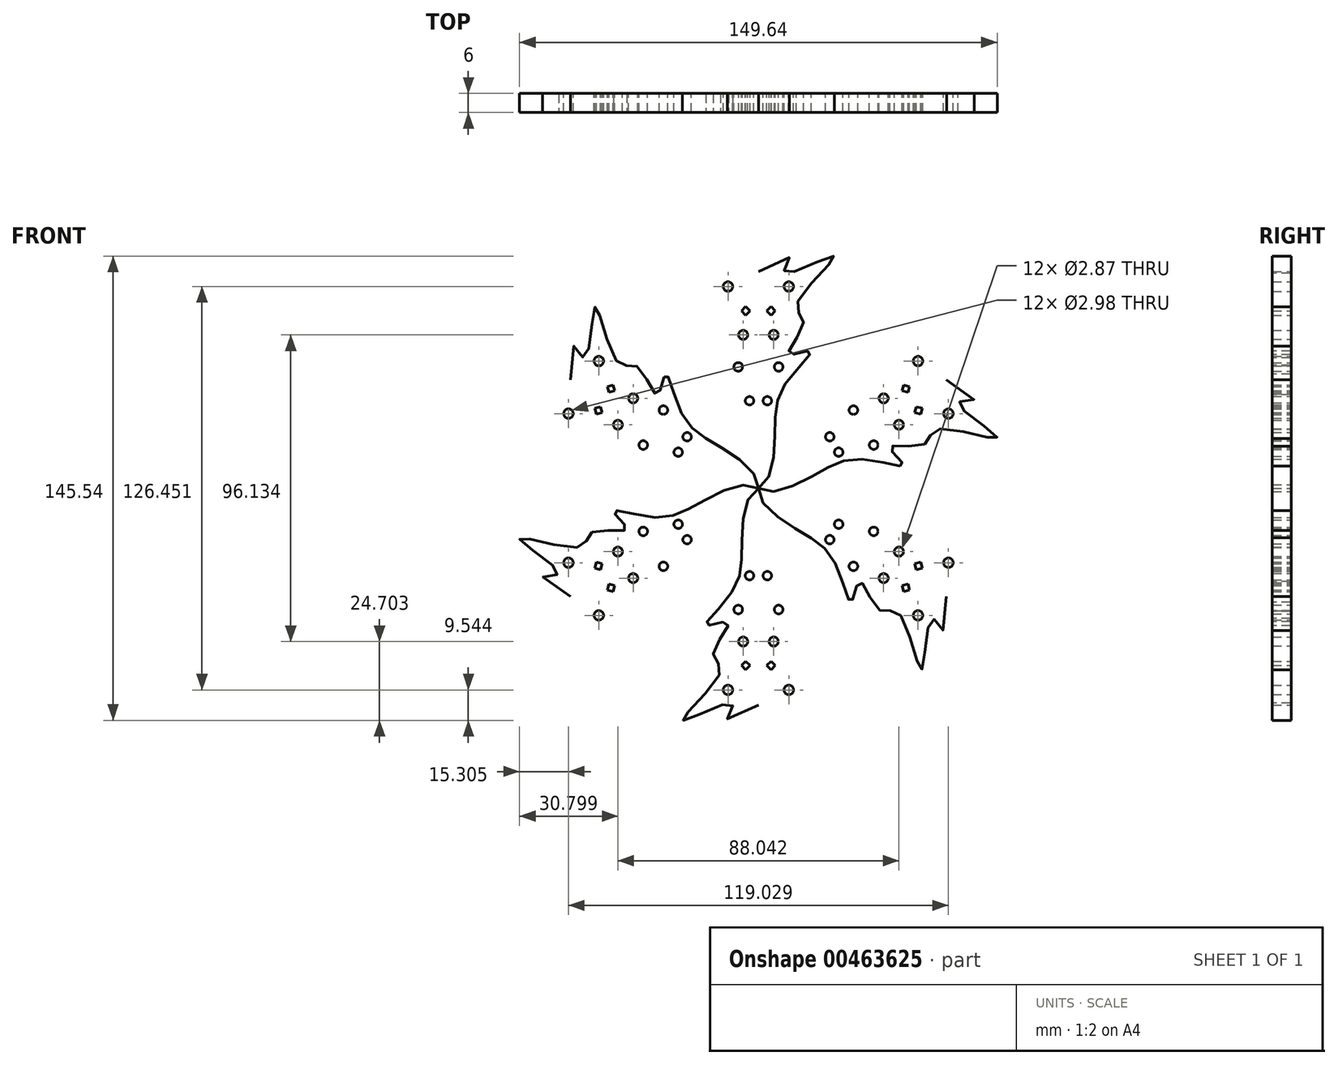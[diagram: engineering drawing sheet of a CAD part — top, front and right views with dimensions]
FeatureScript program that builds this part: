
annotation { "Feature Type Name" : "Feature", "Feature Type Description" : "" }
export const myFeature = defineFeature(function(context is Context, id is Id, definition is map)
    precondition{}
    {
        {
            var Q0;
            Q0=qCreatedBy(makeId("Front.planeOp"),FACE);
            var sketch = newSketch(context, id + "F0", { "sketchPlane" : qUnion([Q0])});
            skLineSegment(sketch, "E0", {"start": v(0, 0) * mm, "end": v(0, 67.96) * mm, "construction": true});
            skFitSpline(sketch, "E1", {"points": [v(0, 67.96) * mm, v(8.04, 67.96) * mm, v(23.58, 72.76) * mm, v(11.93, 57.55) * mm, v(14.13, 51.98) * mm, v(9.52, 42.08) * mm, v(16.32, 43.03) * mm, v(8.31, 32.65) * mm, v(5.2, 16.68) * mm, v(0, 0) * mm], "startDerivative": vector(501.65, 313.3) * mm, "endDerivative": vector(-99, -40.62) * mm});
            skCircle(sketch, "E2", {"center": v(4.79, 48.07) * mm, "radius": 1.43 * mm});
            skCircle(sketch, "E3", {"center": v(6.33, 38.02) * mm, "radius": 1.36 * mm});
            skCircle(sketch, "E4", {"center": v(9.52, 63.23) * mm, "radius": 1.49 * mm});
            skCircle(sketch, "E5", {"center": v(2.79, 27.41) * mm, "radius": 1.33 * mm});
            skLineSegment(sketch, "E6.bottom", {"start": v(3.95, 56.95) * mm, "end": v(5.3, 55.6) * mm});
            skLineSegment(sketch, "E6.top", {"start": v(2.6, 55.6) * mm, "end": v(3.96, 54.24) * mm});
            skLineSegment(sketch, "E6.left", {"start": v(3.95, 56.95) * mm, "end": v(2.6, 55.6) * mm});
            skLineSegment(sketch, "E6.right", {"start": v(5.3, 55.6) * mm, "end": v(3.96, 54.24) * mm});
            skFitSpline(sketch, "E7.MirrorCS", {"points": [v(0, 67.96) * mm, v(-8.04, 67.96) * mm, v(-23.58, 72.76) * mm, v(-11.93, 57.55) * mm, v(-14.13, 51.98) * mm, v(-9.52, 42.08) * mm, v(-16.32, 43.03) * mm, v(-8.31, 32.65) * mm, v(-5.2, 16.68) * mm, v(0, 0) * mm], "startDerivative": vector(-501.65, 313.3) * mm, "endDerivative": vector(99, -40.62) * mm});
            skCircle(sketch, "E8.MirrorC", {"center": v(-9.52, 63.23) * mm, "radius": 1.49 * mm});
            skCircle(sketch, "E9.MirrorC", {"center": v(-4.79, 48.07) * mm, "radius": 1.43 * mm});
            skCircle(sketch, "E10.MirrorC", {"center": v(-6.33, 38.02) * mm, "radius": 1.36 * mm});
            skCircle(sketch, "E11.MirrorC", {"center": v(-2.79, 27.41) * mm, "radius": 1.33 * mm});
            skLineSegment(sketch, "E12.MirrorCS", {"start": v(-2.6, 55.6) * mm, "end": v(-3.96, 54.24) * mm});
            skLineSegment(sketch, "E13.MirrorCS", {"start": v(-3.95, 56.95) * mm, "end": v(-2.6, 55.6) * mm});
            skLineSegment(sketch, "E14.MirrorCS", {"start": v(-3.95, 56.95) * mm, "end": v(-5.3, 55.6) * mm});
            skLineSegment(sketch, "E15.MirrorCS", {"start": v(-5.3, 55.6) * mm, "end": v(-3.96, 54.24) * mm});
            skSolve(sketch);
        }
        {
            var Q0;
            Q0 = qSketchRegion(id + "F0", true);
            extrude(context, id + "F1", {"entities" : qUnion([Q0]), "depth" : 6 * mm});
        }
        {
            var Q0;
            Q0=qCreatedBy(makeId("Right.planeOp"),FACE);
            var sketch = newSketch(context, id + "F2", { "sketchPlane" : qUnion([Q0])});
            skLineSegment(sketch, "E16", {"start": v(0, 0) * mm, "end": v(-58.84, 0) * mm, "construction": true});
            skSolve(sketch);
        }
        {
            var Q0;
            Q0=makeQuery(id+"F1.opExtrude","SWEPT_BODY",BODY,{"disambiguationData":[OSD([sQuery(id+"F0.wireOp",EDGE,"E1"),sQuery(id+"F0.wireOp",EDGE,"E2"),sQuery(id+"F0.wireOp",EDGE,"E3"),sQuery(id+"F0.wireOp",EDGE,"E4"),sQuery(id+"F0.wireOp",EDGE,"E5"),sQuery(id+"F0.wireOp",EDGE,"E6.bottom"),sQuery(id+"F0.wireOp",EDGE,"E6.top"),sQuery(id+"F0.wireOp",EDGE,"E6.left"),sQuery(id+"F0.wireOp",EDGE,"E6.right"),sQuery(id+"F0.wireOp",EDGE,"E7.MirrorCS"),sQuery(id+"F0.wireOp",EDGE,"E8.MirrorC"),sQuery(id+"F0.wireOp",EDGE,"E9.MirrorC"),sQuery(id+"F0.wireOp",EDGE,"E10.MirrorC"),sQuery(id+"F0.wireOp",EDGE,"E11.MirrorC"),sQuery(id+"F0.wireOp",EDGE,"E12.MirrorCS"),sQuery(id+"F0.wireOp",EDGE,"E13.MirrorCS"),sQuery(id+"F0.wireOp",EDGE,"E14.MirrorCS"),sQuery(id+"F0.wireOp",EDGE,"E15.MirrorCS")])]});
            var Q1;
            Q1=sQuery(id+"F2.wireOp",EDGE,"E16");
            circularPattern(context, id + "F3", {"entities" : qUnion([Q0]), "axis" : qUnion([Q1]), "angle" : 360 * degree, "instanceCount" : 6, "equalSpace" : true});
        }
    });
